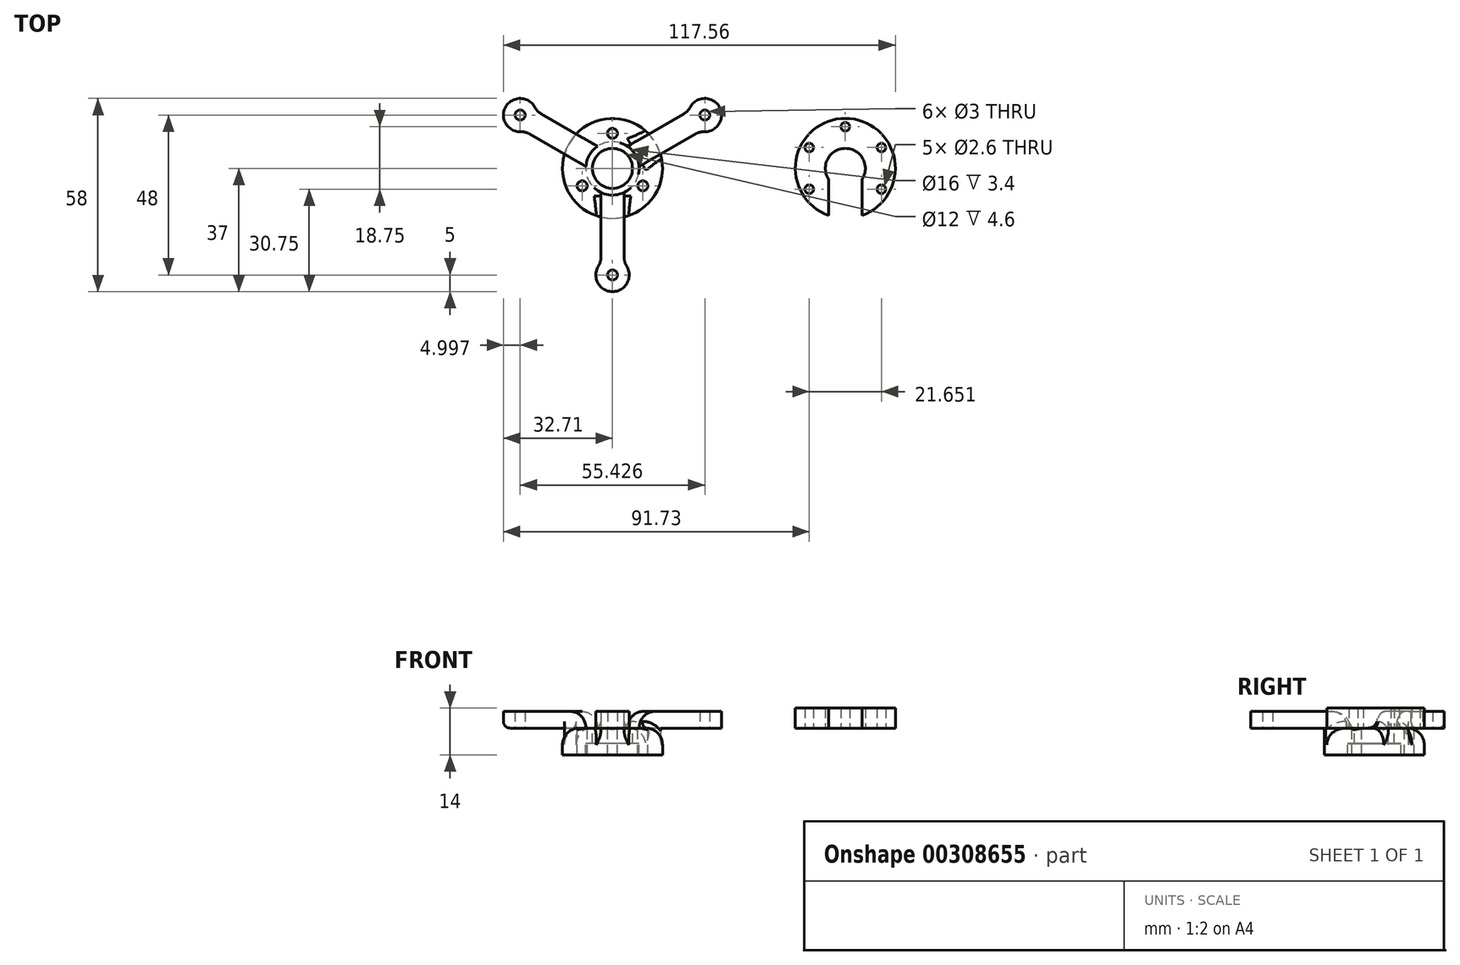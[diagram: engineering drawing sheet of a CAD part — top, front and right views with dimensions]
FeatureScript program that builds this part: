
annotation { "Feature Type Name" : "Feature", "Feature Type Description" : "" }
export const myFeature = defineFeature(function(context is Context, id is Id, definition is map)
    precondition{}
    {
        {
            var Q0;
            Q0=qCreatedBy(makeId("Top.planeOp"),FACE);
            var sketch = newSketch(context, id + "F0", { "sketchPlane" : qUnion([Q0])});
            skCircle(sketch, "E0", {"center": v(0, 0) * mm, "radius": 32 * mm});
            skLineSegment(sketch, "E1", {"start": v(5.2, 3) * mm, "end": v(27.71, 16) * mm});
            skCircle(sketch, "E2", {"center": v(27.71, 16) * mm, "radius": 1.5 * mm});
            skCircle(sketch, "E3", {"center": v(27.71, 16) * mm, "radius": 5 * mm});
            skLineSegment(sketch, "E4", {"start": v(25.11, 14.5) * mm, "end": v(23.36, 17.53) * mm});
            skLineSegment(sketch, "E5", {"start": v(23.36, 17.53) * mm, "end": v(20.33, 15.78) * mm});
            skLineSegment(sketch, "E6", {"start": v(20.33, 15.78) * mm, "end": v(22.08, 12.75) * mm});
            skLineSegment(sketch, "E7.MirrorCS", {"start": v(26.86, 11.47) * mm, "end": v(23.83, 9.72) * mm});
            skLineSegment(sketch, "E8.MirrorCS", {"start": v(23.83, 9.72) * mm, "end": v(22.08, 12.75) * mm});
            skLineSegment(sketch, "E9.MirrorCS", {"start": v(25.11, 14.5) * mm, "end": v(26.86, 11.47) * mm});
            skCircle(sketch, "E10.1.0", {"center": v(-27.71, 16) * mm, "radius": 5 * mm});
            skCircle(sketch, "E10.1.1", {"center": v(-27.71, 16) * mm, "radius": 1.5 * mm});
            skLineSegment(sketch, "E10.1.2", {"start": v(-25.11, 14.5) * mm, "end": v(-26.86, 11.47) * mm});
            skLineSegment(sketch, "E10.1.3", {"start": v(-25.11, 14.5) * mm, "end": v(-23.36, 17.53) * mm});
            skLineSegment(sketch, "E10.1.4", {"start": v(-23.36, 17.53) * mm, "end": v(-20.33, 15.78) * mm});
            skLineSegment(sketch, "E10.1.5", {"start": v(-20.33, 15.78) * mm, "end": v(-22.08, 12.75) * mm});
            skLineSegment(sketch, "E10.1.6", {"start": v(-23.83, 9.72) * mm, "end": v(-22.08, 12.75) * mm});
            skLineSegment(sketch, "E10.1.7", {"start": v(-26.86, 11.47) * mm, "end": v(-23.83, 9.72) * mm});
            skCircle(sketch, "E10.2.0", {"center": v(0, -32) * mm, "radius": 5 * mm});
            skCircle(sketch, "E10.2.1", {"center": v(0, -32) * mm, "radius": 1.5 * mm});
            skLineSegment(sketch, "E10.2.2", {"start": v(0, -29) * mm, "end": v(3.5, -29) * mm});
            skLineSegment(sketch, "E10.2.3", {"start": v(0, -29) * mm, "end": v(-3.5, -29) * mm});
            skLineSegment(sketch, "E10.2.4", {"start": v(-3.5, -29) * mm, "end": v(-3.5, -25.5) * mm});
            skLineSegment(sketch, "E10.2.5", {"start": v(-3.5, -25.5) * mm, "end": v(0, -25.5) * mm});
            skLineSegment(sketch, "E10.2.6", {"start": v(3.5, -25.5) * mm, "end": v(0, -25.5) * mm});
            skLineSegment(sketch, "E10.2.7", {"start": v(3.5, -29) * mm, "end": v(3.5, -25.5) * mm});
            skLineSegment(sketch, "E11.0", {"start": v(5.97, -0.6) * mm, "end": v(29.3, 12.87) * mm});
            skLineSegment(sketch, "E12.0", {"start": v(2.47, 5.47) * mm, "end": v(25.8, 18.94) * mm});
            skCircle(sketch, "E13", {"center": v(0, 0) * mm, "radius": 6 * mm});
            skCircle(sketch, "E14", {"center": v(0, 0) * mm, "radius": 8 * mm});
            skCircle(sketch, "E15", {"center": v(0, 0) * mm, "radius": 15 * mm});
            skLineSegment(sketch, "E16", {"start": v(-32.04, 13.5) * mm, "end": v(-4.33, -34.5) * mm});
            skLineSegment(sketch, "E17", {"start": v(-18.19, -10.5) * mm, "end": v(-16.45, -9.5) * mm});
            skCircle(sketch, "E18", {"center": v(0, 0) * mm, "radius": 25 * mm});
            skCircle(sketch, "E19", {"center": v(0, 10.5) * mm, "radius": 1.5 * mm});
            skCircle(sketch, "E20.1.0", {"center": v(-9.1, -5.25) * mm, "radius": 1.5 * mm});
            skCircle(sketch, "E20.2.0", {"center": v(9.1, -5.25) * mm, "radius": 1.5 * mm});
            skCircle(sketch, "E21", {"center": v(69.85, 0) * mm, "radius": 6 * mm});
            skCircle(sketch, "E22", {"center": v(69.85, 0) * mm, "radius": 15 * mm});
            skCircle(sketch, "E23", {"center": v(69.85, 12.5) * mm, "radius": 1.3 * mm});
            skCircle(sketch, "E24.1.0", {"center": v(59.02, 6.25) * mm, "radius": 1.3 * mm});
            skCircle(sketch, "E24.2.0", {"center": v(59.02, -6.25) * mm, "radius": 1.3 * mm});
            skLineSegment(sketch, "E25", {"start": v(69.85, -6) * mm, "end": v(69.85, -15) * mm});
            skLineSegment(sketch, "E26.0", {"start": v(64.85, -3.32) * mm, "end": v(64.85, -14.14) * mm});
            skLineSegment(sketch, "E27.0", {"start": v(74.85, -3.32) * mm, "end": v(74.85, -14.14) * mm});
            skCircle(sketch, "E28.1.4.0", {"center": v(80.67, -6.25) * mm, "radius": 1.3 * mm});
            skCircle(sketch, "E29.1.5.0", {"center": v(80.67, 6.25) * mm, "radius": 1.3 * mm});
            skSolve(sketch);
        }
        {
            var Q0;
            {var subQ0=sQuery(id+"F0.wireOp",EDGE,"E3");var subQ1=sQuery(id+"F0.wireOp",EDGE,"E0");var subQ2=makeQuery(id+"F0.imprint","INTERSECT",VERTEX,{"disambiguationData":[OD(0.0)],"derivedFrom":[subQ1,subQ0]});Q0=makeQuery(id+"F0.imprint","IMPRINT",FACE,{"disambiguationData":[TD([[makeQuery(id+"F0.imprint","IMPRINT",EDGE,{"disambiguationData":[TD([[subQ2,-1.0]])],"derivedFrom":subQ1}),-1.0]])]});}
            var Q1;
            {var subQ9=sQuery(id+"F0.wireOp",EDGE,"E4");Q1=makeQuery(id+"F0.imprint","IMPRINT",FACE,{"disambiguationData":[TD([[makeQuery(id+"F0.imprint","IMPRINT",EDGE,{"derivedFrom":subQ9}),-1.0]])]});}
            var Q2;
            {var subQ9=sQuery(id+"F0.wireOp",EDGE,"E9.MirrorCS");Q2=makeQuery(id+"F0.imprint","IMPRINT",FACE,{"disambiguationData":[TD([[makeQuery(id+"F0.imprint","IMPRINT",EDGE,{"derivedFrom":subQ9}),1.0]])]});}
            var Q3;
            {var subQ0=sQuery(id+"F0.wireOp",EDGE,"E9.MirrorCS");Q3=makeQuery(id+"F0.imprint","IMPRINT",FACE,{"disambiguationData":[TD([[makeQuery(id+"F0.imprint","IMPRINT",EDGE,{"derivedFrom":subQ0}),-1.0]])]});}
            var Q4;
            {var subQ0=sQuery(id+"F0.wireOp",EDGE,"E4");Q4=makeQuery(id+"F0.imprint","IMPRINT",FACE,{"disambiguationData":[TD([[makeQuery(id+"F0.imprint","IMPRINT",EDGE,{"derivedFrom":subQ0}),1.0]])]});}
            var Q5;
            {var subQ0=sQuery(id+"F0.wireOp",EDGE,"E11.0");var subQ1=sQuery(id+"F0.wireOp",EDGE,"E0");var subQ2=makeQuery(id+"F0.imprint","INTERSECT",VERTEX,{"derivedFrom":[subQ1,subQ0]});Q5=makeQuery(id+"F0.imprint","IMPRINT",FACE,{"disambiguationData":[TD([[makeQuery(id+"F0.imprint","IMPRINT",EDGE,{"disambiguationData":[TD([[subQ2,1.0]])],"derivedFrom":subQ1}),1.0]])]});}
            var Q6;
            {var subQ0=sQuery(id+"F0.wireOp",EDGE,"E12.0");var subQ1=sQuery(id+"F0.wireOp",EDGE,"E0");var subQ2=makeQuery(id+"F0.imprint","INTERSECT",VERTEX,{"derivedFrom":[subQ1,subQ0]});Q6=makeQuery(id+"F0.imprint","IMPRINT",FACE,{"disambiguationData":[TD([[makeQuery(id+"F0.imprint","IMPRINT",EDGE,{"disambiguationData":[TD([[subQ2,-1.0]])],"derivedFrom":subQ1}),1.0]])]});}
            extrude(context, id + "F1", {"entities" : qUnion([Q0, Q1, Q2, Q3, Q4, Q5, Q6]), "depth" : 5 * mm});
        }
        {
            var Q0;
            {var subQ0=sQuery(id+"F0.wireOp",EDGE,"E8.MirrorCS");Q0=makeQuery(id+"F0.imprint","IMPRINT",FACE,{"disambiguationData":[TD([[makeQuery(id+"F0.imprint","IMPRINT",EDGE,{"derivedFrom":subQ0}),-1.0]])]});}
            var Q1;
            {var subQ0=sQuery(id+"F0.wireOp",EDGE,"E6");Q1=makeQuery(id+"F0.imprint","IMPRINT",FACE,{"disambiguationData":[TD([[makeQuery(id+"F0.imprint","IMPRINT",EDGE,{"derivedFrom":subQ0}),1.0]])]});}
            var Q2;
            {var subQ0=sQuery(id+"F0.wireOp",EDGE,"E9.MirrorCS");Q2=makeQuery(id+"F0.imprint","IMPRINT",FACE,{"disambiguationData":[TD([[makeQuery(id+"F0.imprint","IMPRINT",EDGE,{"derivedFrom":subQ0}),-1.0]])]});}
            var Q3;
            {var subQ0=sQuery(id+"F0.wireOp",EDGE,"E4");Q3=makeQuery(id+"F0.imprint","IMPRINT",FACE,{"disambiguationData":[TD([[makeQuery(id+"F0.imprint","IMPRINT",EDGE,{"derivedFrom":subQ0}),1.0]])]});}
            var Q4;
            {var subQ0=sQuery(id+"F0.wireOp",EDGE,"E6");Q4=makeQuery(id+"F0.imprint","IMPRINT",FACE,{"disambiguationData":[TD([[makeQuery(id+"F0.imprint","IMPRINT",EDGE,{"derivedFrom":subQ0}),-1.0]])]});}
            var Q5;
            {var subQ0=sQuery(id+"F0.wireOp",EDGE,"E8.MirrorCS");Q5=makeQuery(id+"F0.imprint","IMPRINT",FACE,{"disambiguationData":[TD([[makeQuery(id+"F0.imprint","IMPRINT",EDGE,{"derivedFrom":subQ0}),1.0]])]});}
            var Q6;
            {var subQ0=sQuery(id+"F0.wireOp",EDGE,"E15");var subQ1=sQuery(id+"F0.wireOp",EDGE,"E1");var subQ2=makeQuery(id+"F0.imprint","INTERSECT",VERTEX,{"derivedFrom":[subQ1,subQ0]});Q6=makeQuery(id+"F0.imprint","IMPRINT",FACE,{"disambiguationData":[TD([[makeQuery(id+"F0.imprint","IMPRINT",EDGE,{"disambiguationData":[TD([[subQ2,-1.0]])],"derivedFrom":subQ1}),-1.0]])]});}
            var Q7;
            {var subQ0=sQuery(id+"F0.wireOp",EDGE,"E15");var subQ1=sQuery(id+"F0.wireOp",EDGE,"E1");var subQ2=makeQuery(id+"F0.imprint","INTERSECT",VERTEX,{"derivedFrom":[subQ1,subQ0]});Q7=makeQuery(id+"F0.imprint","IMPRINT",FACE,{"disambiguationData":[TD([[makeQuery(id+"F0.imprint","IMPRINT",EDGE,{"disambiguationData":[TD([[subQ2,-1.0]])],"derivedFrom":subQ1}),1.0]])]});}
            var Q8;
            {var subQ0=sQuery(id+"F0.wireOp",EDGE,"E14");var subQ1=sQuery(id+"F0.wireOp",EDGE,"E1");var subQ2=makeQuery(id+"F0.imprint","INTERSECT",VERTEX,{"derivedFrom":[subQ1,subQ0]});Q8=makeQuery(id+"F0.imprint","IMPRINT",FACE,{"disambiguationData":[TD([[makeQuery(id+"F0.imprint","IMPRINT",EDGE,{"disambiguationData":[TD([[subQ2,-1.0]])],"derivedFrom":subQ1}),1.0]])]});}
            var Q9;
            {var subQ0=sQuery(id+"F0.wireOp",EDGE,"E14");var subQ1=sQuery(id+"F0.wireOp",EDGE,"E1");var subQ2=makeQuery(id+"F0.imprint","INTERSECT",VERTEX,{"derivedFrom":[subQ1,subQ0]});Q9=makeQuery(id+"F0.imprint","IMPRINT",FACE,{"disambiguationData":[TD([[makeQuery(id+"F0.imprint","IMPRINT",EDGE,{"disambiguationData":[TD([[subQ2,-1.0]])],"derivedFrom":subQ1}),-1.0]])]});}
            extrude(context, id + "F2", {"entities" : qUnion([Q0, Q1, Q2, Q3, Q4, Q5, Q6, Q7, Q8, Q9]), "operationType" : NewBodyOperationType.ADD, "depth" : 5 * mm});
        }
        {
            var Q0;
            {var subQ0=sQuery(id+"F0.wireOp",EDGE,"E14");var subQ1=sQuery(id+"F0.wireOp",EDGE,"E1");var subQ2=makeQuery(id+"F0.imprint","INTERSECT",VERTEX,{"derivedFrom":[subQ1,subQ0]});Q0=makeQuery(id+"F0.imprint","IMPRINT",FACE,{"disambiguationData":[TD([[makeQuery(id+"F0.imprint","IMPRINT",EDGE,{"disambiguationData":[TD([[subQ2,-1.0]])],"derivedFrom":subQ1}),1.0]])]});}
            var Q1;
            {var subQ0=sQuery(id+"F0.wireOp",EDGE,"E14");var subQ1=sQuery(id+"F0.wireOp",EDGE,"E1");var subQ2=makeQuery(id+"F0.imprint","INTERSECT",VERTEX,{"derivedFrom":[subQ1,subQ0]});Q1=makeQuery(id+"F0.imprint","IMPRINT",FACE,{"disambiguationData":[TD([[makeQuery(id+"F0.imprint","IMPRINT",EDGE,{"disambiguationData":[TD([[subQ2,-1.0]])],"derivedFrom":subQ1}),-1.0]])]});}
            var Q2;
            {var subQ0=sQuery(id+"F0.wireOp",EDGE,"E14");var subQ1=sQuery(id+"F0.wireOp",EDGE,"E11.0");var subQ2=makeQuery(id+"F0.imprint","INTERSECT",VERTEX,{"derivedFrom":[subQ1,subQ0]});Q2=makeQuery(id+"F0.imprint","IMPRINT",FACE,{"disambiguationData":[TD([[makeQuery(id+"F0.imprint","IMPRINT",EDGE,{"disambiguationData":[TD([[subQ2,-1.0]])],"derivedFrom":subQ1}),-1.0]])]});}
            extrude(context, id + "F3", {"entities" : qUnion([Q0, Q1, Q2]), "oppositeDirection" : true, "depth" : 8 * mm});
        }
        {
            var Q0;
            Q0=makeQuery(id+"F1.opExtrude","SWEPT_BODY",BODY,{"disambiguationData":[OSD([sQuery(id+"F0.wireOp",EDGE,"E2"),sQuery(id+"F0.wireOp",EDGE,"E3")])]});
            var Q1;
            Q1=sQuery(id+"F0.wireOp",EDGE,"E0");
            circularPattern(context, id + "F4", {"entities" : qUnion([Q0]), "axis" : qUnion([Q1]), "angle" : 360 * degree, "instanceCount" : 3, "equalSpace" : true});
        }
        {
            var Q0;
            {var subQ0=sQuery(id+"F0.wireOp",EDGE,"E13");var subQ1=sQuery(id+"F0.wireOp",EDGE,"E11.0");var subQ2=makeQuery(id+"F0.imprint","INTERSECT",VERTEX,{"derivedFrom":[subQ1,subQ0]});Q0=makeQuery(id+"F0.imprint","IMPRINT",FACE,{"disambiguationData":[TD([[makeQuery(id+"F0.imprint","IMPRINT",EDGE,{"disambiguationData":[TD([[subQ2,-1.0]])],"derivedFrom":subQ1}),-1.0]])]});}
            var Q1;
            {var subQ0=sQuery(id+"F0.wireOp",EDGE,"E13");var subQ1=sQuery(id+"F0.wireOp",EDGE,"E1");var subQ2=makeQuery(id+"F0.imprint","INTERSECT",VERTEX,{"derivedFrom":[subQ1,subQ0]});Q1=makeQuery(id+"F0.imprint","IMPRINT",FACE,{"disambiguationData":[TD([[makeQuery(id+"F0.imprint","IMPRINT",EDGE,{"disambiguationData":[TD([[subQ2,-1.0]])],"derivedFrom":subQ1}),1.0]])]});}
            var Q2;
            {var subQ0=sQuery(id+"F0.wireOp",EDGE,"E13");var subQ1=sQuery(id+"F0.wireOp",EDGE,"E1");var subQ2=makeQuery(id+"F0.imprint","INTERSECT",VERTEX,{"derivedFrom":[subQ1,subQ0]});Q2=makeQuery(id+"F0.imprint","IMPRINT",FACE,{"disambiguationData":[TD([[makeQuery(id+"F0.imprint","IMPRINT",EDGE,{"disambiguationData":[TD([[subQ2,-1.0]])],"derivedFrom":subQ1}),-1.0]])]});}
            extrude(context, id + "F5", {"entities" : qUnion([Q0, Q1, Q2]), "oppositeDirection" : true, "depth" : 4.6 * mm});
        }
        {
            var Q0;
            Q0=makeQuery(id+"F4.opPattern","COPY",EDGE,{"derivedFrom":makeQuery(id+"F2.boolean.opBoolean","INTERSECT",EDGE,{"derivedFrom":[makeQuery(id+"F1.opExtrude","SWEPT_FACE",FACE,{"disambiguationData":[OSD([sQuery(id+"F0.wireOp",EDGE,"E3")])]}),makeQuery(id+"F2.opExtrude","SWEPT_FACE",FACE,{"disambiguationData":[OSD([sQuery(id+"F0.wireOp",EDGE,"E12.0")])]})]}),"instanceName":"2"});
            var Q1;
            Q1=makeQuery(id+"F4.opPattern","COPY",EDGE,{"derivedFrom":makeQuery(id+"F2.boolean.opBoolean","INTERSECT",EDGE,{"derivedFrom":[makeQuery(id+"F1.opExtrude","SWEPT_FACE",FACE,{"disambiguationData":[OSD([sQuery(id+"F0.wireOp",EDGE,"E3")])]}),makeQuery(id+"F2.opExtrude","SWEPT_FACE",FACE,{"disambiguationData":[OSD([sQuery(id+"F0.wireOp",EDGE,"E11.0")])]})]}),"instanceName":"2"});
            var Q2;
            Q2=makeQuery(id+"F2.boolean.opBoolean","INTERSECT",EDGE,{"derivedFrom":[makeQuery(id+"F1.opExtrude","SWEPT_FACE",FACE,{"disambiguationData":[OSD([sQuery(id+"F0.wireOp",EDGE,"E3")])]}),makeQuery(id+"F2.opExtrude","SWEPT_FACE",FACE,{"disambiguationData":[OSD([sQuery(id+"F0.wireOp",EDGE,"E11.0")])]})]});
            var Q3;
            Q3=makeQuery(id+"F2.boolean.opBoolean","INTERSECT",EDGE,{"derivedFrom":[makeQuery(id+"F1.opExtrude","SWEPT_FACE",FACE,{"disambiguationData":[OSD([sQuery(id+"F0.wireOp",EDGE,"E3")])]}),makeQuery(id+"F2.opExtrude","SWEPT_FACE",FACE,{"disambiguationData":[OSD([sQuery(id+"F0.wireOp",EDGE,"E12.0")])]})]});
            var Q4;
            Q4=makeQuery(id+"F4.opPattern","COPY",EDGE,{"derivedFrom":makeQuery(id+"F2.boolean.opBoolean","INTERSECT",EDGE,{"derivedFrom":[makeQuery(id+"F1.opExtrude","SWEPT_FACE",FACE,{"disambiguationData":[OSD([sQuery(id+"F0.wireOp",EDGE,"E3")])]}),makeQuery(id+"F2.opExtrude","SWEPT_FACE",FACE,{"disambiguationData":[OSD([sQuery(id+"F0.wireOp",EDGE,"E11.0")])]})]}),"instanceName":"1"});
            var Q5;
            Q5=makeQuery(id+"F4.opPattern","COPY",EDGE,{"derivedFrom":makeQuery(id+"F2.boolean.opBoolean","INTERSECT",EDGE,{"derivedFrom":[makeQuery(id+"F1.opExtrude","SWEPT_FACE",FACE,{"disambiguationData":[OSD([sQuery(id+"F0.wireOp",EDGE,"E3")])]}),makeQuery(id+"F2.opExtrude","SWEPT_FACE",FACE,{"disambiguationData":[OSD([sQuery(id+"F0.wireOp",EDGE,"E12.0")])]})]}),"instanceName":"1"});
            fillet(context, id + "F6", {"entities" : qUnion([Q0, Q1, Q2, Q3, Q4, Q5]), "radius" : 5 * mm, "tangentPropagation" : true, "allowEdgeOverflow" : false});
        }
        {
            var Q0;
            Q0=makeQuery(id+"F0.imprint","IMPRINT",FACE,{"disambiguationData":[TD([[makeQuery(id+"F0.imprint","IMPRINT",EDGE,{"derivedFrom":sQuery(id+"F0.wireOp",EDGE,"E23")}),-1.0]])]});
            extrude(context, id + "F7", {"entities" : qUnion([Q0]), "depth" : 6 * mm});
        }
        {
            var Q0;
            Q0=makeQuery(id+"F4.opPattern","COPY",BODY,{"derivedFrom":makeQuery(id+"F1.opExtrude","SWEPT_BODY",BODY,{"disambiguationData":[OSD([sQuery(id+"F0.wireOp",EDGE,"E2"),sQuery(id+"F0.wireOp",EDGE,"E3")])]}),"instanceName":"1"});
            var Q1;
            Q1=makeQuery(id+"F1.opExtrude","SWEPT_BODY",BODY,{"disambiguationData":[OSD([sQuery(id+"F0.wireOp",EDGE,"E2"),sQuery(id+"F0.wireOp",EDGE,"E3")])]});
            var Q2;
            Q2=makeQuery(id+"F4.opPattern","COPY",BODY,{"derivedFrom":makeQuery(id+"F1.opExtrude","SWEPT_BODY",BODY,{"disambiguationData":[OSD([sQuery(id+"F0.wireOp",EDGE,"E2"),sQuery(id+"F0.wireOp",EDGE,"E3")])]}),"instanceName":"2"});
            var Q3;
            Q3=makeQuery(id+"F3.opExtrude","SWEPT_BODY",BODY,{"disambiguationData":[OSD([sQuery(id+"F0.wireOp",EDGE,"E14"),sQuery(id+"F0.wireOp",EDGE,"E15"),sQuery(id+"F0.wireOp",EDGE,"E19"),sQuery(id+"F0.wireOp",EDGE,"E20.1.0"),sQuery(id+"F0.wireOp",EDGE,"E20.2.0")])]});
            var Q4;
            Q4=makeQuery(id+"F5.opExtrude","SWEPT_BODY",BODY,{"disambiguationData":[OSD([sQuery(id+"F0.wireOp",EDGE,"E13"),sQuery(id+"F0.wireOp",EDGE,"E14")])]});
            booleanBodies(context, id + "F8", {"operationType" : BooleanOperationType.UNION, "tools" : qUnion([Q0, Q1, Q2, Q3, Q4])});
        }
        {
            var Q0;
            Q0=makeQuery(id+"F4.opPattern","COPY",EDGE,{"derivedFrom":makeQuery(id+"F2.opExtrude","CAP_EDGE",EDGE,{"disambiguationData":[OSD([sQuery(id+"F0.wireOp",EDGE,"E14")])],"isStart":false}),"instanceName":"1"});
            var Q1;
            Q1=makeQuery(id+"F2.opExtrude","CAP_EDGE",EDGE,{"disambiguationData":[OSD([sQuery(id+"F0.wireOp",EDGE,"E14")])],"isStart":false});
            var Q2;
            Q2=makeQuery(id+"F4.opPattern","COPY",EDGE,{"derivedFrom":makeQuery(id+"F2.opExtrude","CAP_EDGE",EDGE,{"disambiguationData":[OSD([sQuery(id+"F0.wireOp",EDGE,"E14")])],"isStart":false}),"instanceName":"2"});
            fillet(context, id + "F9", {"entities" : qUnion([Q0, Q1, Q2]), "radius" : 5 * mm, "tangentPropagation" : true, "allowEdgeOverflow" : false});
        }
        {
            var Q0;
            {var subQ0=sQuery(id+"F0.wireOp",EDGE,"E15");Q0=makeQuery(id+"F8.opBoolean","SPLIT",EDGE,{"disambiguationData":[topologyDisambiguationEdgeConnected([makeQuery(id+"F1.opExtrude","CAP_FACE",FACE,{"disambiguationData":[OSD([sQuery(id+"F0.wireOp",EDGE,"E2"),sQuery(id+"F0.wireOp",EDGE,"E3")])],"isStart":true}),makeQuery(id+"F2.opExtrude","CAP_FACE",FACE,{"disambiguationData":[OSD([sQuery(id+"F0.wireOp",EDGE,"E4"),sQuery(id+"F0.wireOp",EDGE,"E9.MirrorCS"),sQuery(id+"F0.wireOp",EDGE,"E11.0"),sQuery(id+"F0.wireOp",EDGE,"E12.0"),sQuery(id+"F0.wireOp",EDGE,"E14")])],"isStart":true}),makeQuery(id+"F3.opExtrude","SWEPT_FACE",FACE,{"disambiguationData":[OSD([subQ0])]})])],"derivedFrom":makeQuery(id+"F3.opExtrude","CAP_EDGE",EDGE,{"disambiguationData":[OSD([subQ0])],"isStart":true})});}
            var Q1;
            {var subQ0=sQuery(id+"F0.wireOp",EDGE,"E15");Q1=makeQuery(id+"F8.opBoolean","SPLIT",EDGE,{"disambiguationData":[topologyDisambiguationEdgeConnected([makeQuery(id+"F3.opExtrude","SWEPT_FACE",FACE,{"disambiguationData":[OSD([subQ0])]}),makeQuery(id+"F4.opPattern","COPY",FACE,{"derivedFrom":makeQuery(id+"F2.boolean.opBoolean","MERGE",FACE,{"derivedFrom":[makeQuery(id+"F1.opExtrude","CAP_FACE",FACE,{"disambiguationData":[OSD([sQuery(id+"F0.wireOp",EDGE,"E2"),sQuery(id+"F0.wireOp",EDGE,"E3")])],"isStart":true}),makeQuery(id+"F2.opExtrude","CAP_FACE",FACE,{"disambiguationData":[OSD([sQuery(id+"F0.wireOp",EDGE,"E4"),sQuery(id+"F0.wireOp",EDGE,"E9.MirrorCS"),sQuery(id+"F0.wireOp",EDGE,"E11.0"),sQuery(id+"F0.wireOp",EDGE,"E12.0"),sQuery(id+"F0.wireOp",EDGE,"E14")])],"isStart":true})]}),"instanceName":"2"})])],"derivedFrom":makeQuery(id+"F3.opExtrude","CAP_EDGE",EDGE,{"disambiguationData":[OSD([subQ0])],"isStart":true})});}
            var Q2;
            {var subQ0=sQuery(id+"F0.wireOp",EDGE,"E15");Q2=makeQuery(id+"F8.opBoolean","SPLIT",EDGE,{"disambiguationData":[topologyDisambiguationEdgeConnected([makeQuery(id+"F3.opExtrude","SWEPT_FACE",FACE,{"disambiguationData":[OSD([subQ0])]}),makeQuery(id+"F4.opPattern","COPY",FACE,{"derivedFrom":makeQuery(id+"F2.boolean.opBoolean","MERGE",FACE,{"derivedFrom":[makeQuery(id+"F1.opExtrude","CAP_FACE",FACE,{"disambiguationData":[OSD([sQuery(id+"F0.wireOp",EDGE,"E2"),sQuery(id+"F0.wireOp",EDGE,"E3")])],"isStart":true}),makeQuery(id+"F2.opExtrude","CAP_FACE",FACE,{"disambiguationData":[OSD([sQuery(id+"F0.wireOp",EDGE,"E4"),sQuery(id+"F0.wireOp",EDGE,"E9.MirrorCS"),sQuery(id+"F0.wireOp",EDGE,"E11.0"),sQuery(id+"F0.wireOp",EDGE,"E12.0"),sQuery(id+"F0.wireOp",EDGE,"E14")])],"isStart":true})]}),"instanceName":"1"})])],"derivedFrom":makeQuery(id+"F3.opExtrude","CAP_EDGE",EDGE,{"disambiguationData":[OSD([subQ0])],"isStart":true})});}
            fillet(context, id + "F10", {"entities" : qUnion([Q0, Q1, Q2]), "radius" : 5 * mm, "tangentPropagation" : true, "allowEdgeOverflow" : false});
        }
        {
            var Q0;
            {var subQ0=sQuery(id+"F0.wireOp",EDGE,"E14");var subQ1=sQuery(id+"F0.wireOp",EDGE,"E11.0");Q0=makeQuery(id+"F8.opBoolean","SPLIT",EDGE,{"disambiguationData":[topologyDisambiguationEdgeConnected([makeQuery(id+"F5.opExtrude","CAP_FACE",FACE,{"disambiguationData":[OSD([sQuery(id+"F0.wireOp",EDGE,"E13"),subQ0])],"isStart":true})])],"derivedFrom":makeQuery(id+"F4.opPattern","COPY",EDGE,{"derivedFrom":makeQuery(id+"F2.opExtrude","CAP_EDGE",EDGE,{"disambiguationData":[OSD([subQ1])],"isStart":true}),"instanceName":"2"})});}
            var Q1;
            {var subQ0=sQuery(id+"F0.wireOp",EDGE,"E14");var subQ1=sQuery(id+"F0.wireOp",EDGE,"E12.0");Q1=makeQuery(id+"F8.opBoolean","SPLIT",EDGE,{"disambiguationData":[topologyDisambiguationEdgeConnected([makeQuery(id+"F5.opExtrude","CAP_FACE",FACE,{"disambiguationData":[OSD([sQuery(id+"F0.wireOp",EDGE,"E13"),subQ0])],"isStart":true})])],"derivedFrom":makeQuery(id+"F4.opPattern","COPY",EDGE,{"derivedFrom":makeQuery(id+"F2.opExtrude","CAP_EDGE",EDGE,{"disambiguationData":[OSD([subQ1])],"isStart":true}),"instanceName":"2"})});}
            var Q2;
            {var subQ0=sQuery(id+"F0.wireOp",EDGE,"E14");var subQ1=sQuery(id+"F0.wireOp",EDGE,"E12.0");Q2=makeQuery(id+"F8.opBoolean","SPLIT",EDGE,{"disambiguationData":[topologyDisambiguationEdgeConnected([makeQuery(id+"F5.opExtrude","CAP_FACE",FACE,{"disambiguationData":[OSD([sQuery(id+"F0.wireOp",EDGE,"E13"),subQ0])],"isStart":true})])],"derivedFrom":makeQuery(id+"F4.opPattern","COPY",EDGE,{"derivedFrom":makeQuery(id+"F2.opExtrude","CAP_EDGE",EDGE,{"disambiguationData":[OSD([subQ1])],"isStart":true}),"instanceName":"1"})});}
            var Q3;
            {var subQ0=sQuery(id+"F0.wireOp",EDGE,"E14");var subQ1=sQuery(id+"F0.wireOp",EDGE,"E11.0");Q3=makeQuery(id+"F8.opBoolean","SPLIT",EDGE,{"disambiguationData":[topologyDisambiguationEdgeConnected([makeQuery(id+"F5.opExtrude","CAP_FACE",FACE,{"disambiguationData":[OSD([sQuery(id+"F0.wireOp",EDGE,"E13"),subQ0])],"isStart":true})])],"derivedFrom":makeQuery(id+"F4.opPattern","COPY",EDGE,{"derivedFrom":makeQuery(id+"F2.opExtrude","CAP_EDGE",EDGE,{"disambiguationData":[OSD([subQ1])],"isStart":true}),"instanceName":"1"})});}
            var Q4;
            {var subQ0=sQuery(id+"F0.wireOp",EDGE,"E12.0");var subQ1=sQuery(id+"F0.wireOp",EDGE,"E14");Q4=makeQuery(id+"F8.opBoolean","SPLIT",EDGE,{"disambiguationData":[topologyDisambiguationEdgeConnected([makeQuery(id+"F5.opExtrude","CAP_FACE",FACE,{"disambiguationData":[OSD([sQuery(id+"F0.wireOp",EDGE,"E13"),subQ1])],"isStart":true})])],"derivedFrom":makeQuery(id+"F2.opExtrude","CAP_EDGE",EDGE,{"disambiguationData":[OSD([subQ0])],"isStart":true})});}
            var Q5;
            {var subQ0=sQuery(id+"F0.wireOp",EDGE,"E11.0");var subQ1=sQuery(id+"F0.wireOp",EDGE,"E14");Q5=makeQuery(id+"F8.opBoolean","SPLIT",EDGE,{"disambiguationData":[topologyDisambiguationEdgeConnected([makeQuery(id+"F5.opExtrude","CAP_FACE",FACE,{"disambiguationData":[OSD([sQuery(id+"F0.wireOp",EDGE,"E13"),subQ1])],"isStart":true})])],"derivedFrom":makeQuery(id+"F2.opExtrude","CAP_EDGE",EDGE,{"disambiguationData":[OSD([subQ0])],"isStart":true})});}
            fillet(context, id + "F11", {"entities" : qUnion([Q0, Q1, Q2, Q3, Q4, Q5]), "radius" : 2 * mm, "tangentPropagation" : true, "allowEdgeOverflow" : false});
        }
    });
